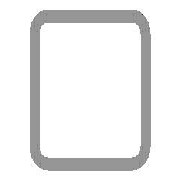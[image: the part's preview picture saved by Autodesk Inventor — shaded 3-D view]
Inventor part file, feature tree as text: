
AUTODESK INVENTOR PART (.ipt)
format: ipt  version: 2019 (Build 230136000, 136)  size: 130,048 bytes
history: native  units: mm (DEFAULTED — no unit token found)
features: other x4, sketch x3, plane x1
ambient origin geometry x8: Origin, YZ Plane, XZ Plane, XY Plane, X Axis, Y Axis, Z Axis, Center Point
bodies: Solid1 (feature_tree), Body (feature_tree)
feature tree (8):
  parser-record x1  (decoder bookkeeping rows leaked as tree rows — omitted from the tree; the rows remain in map.json)
  other  "Driven Length"
  other  "Start plane"
  other  "End plane"
  sketch  "Sketch"  dims[d7=4.0mm d9=20.0mm d11=20.0mm d12=2.0mm d13=-0.0mm d14=300.0mm d15=10.0mm d16=10.0mm d17=90.0deg d18=300.0mm]
  sketch  "Sketch3"  dims[d3=300.0mm]
  plane  "Work Plane3"
  sketch  "Sketch4"  dims[d4=0.0mm]
